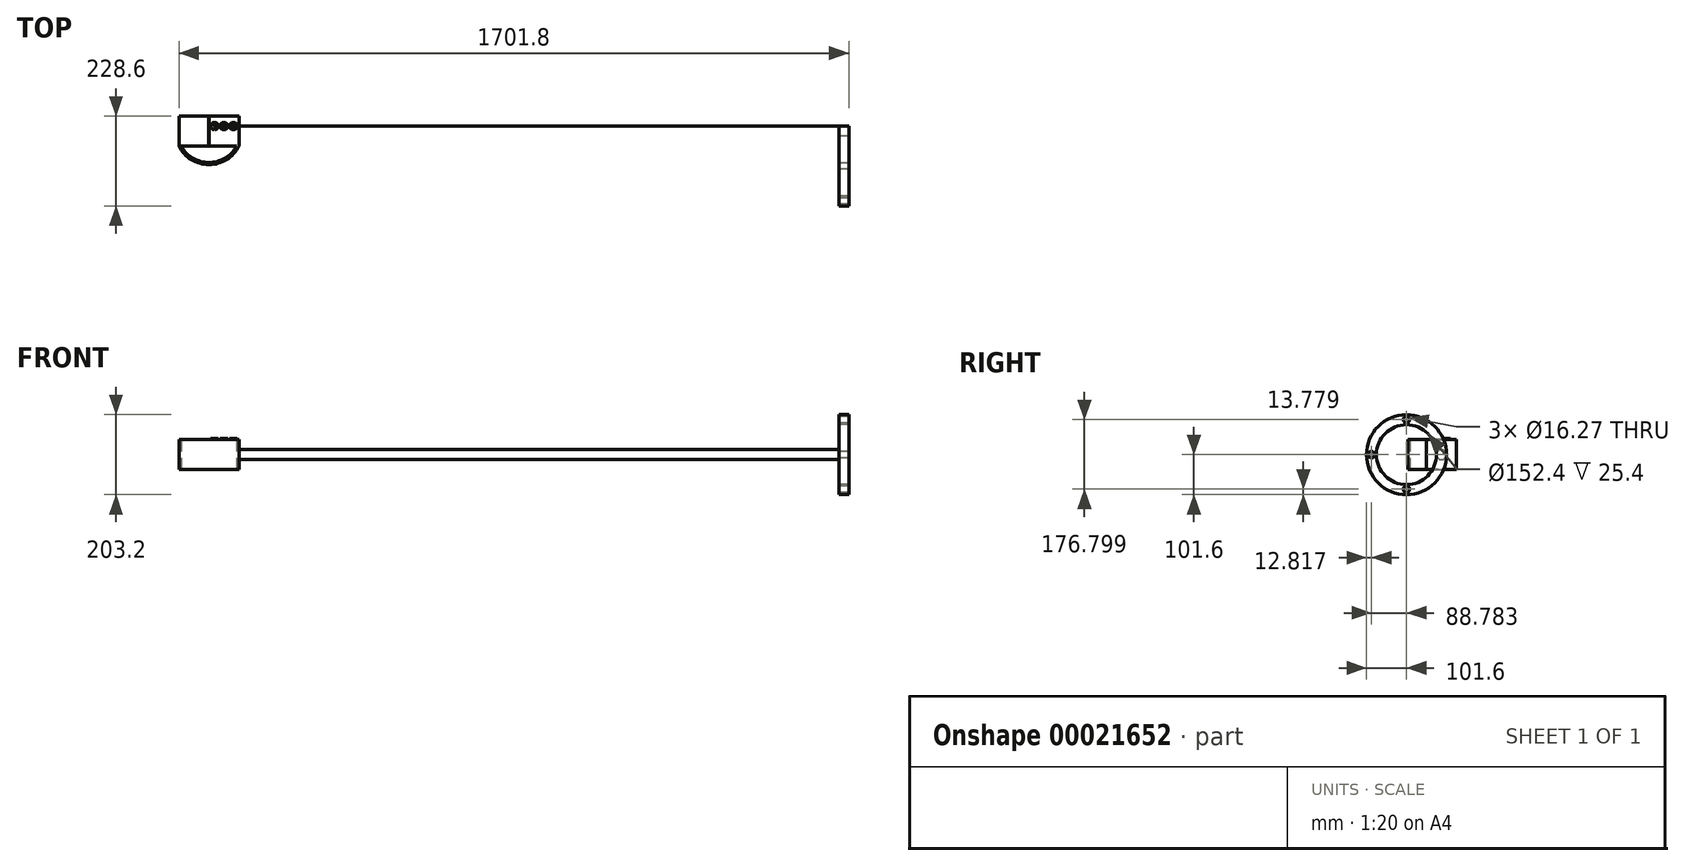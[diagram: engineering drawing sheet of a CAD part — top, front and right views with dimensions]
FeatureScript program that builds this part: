
annotation { "Feature Type Name" : "Feature", "Feature Type Description" : "" }
export const myFeature = defineFeature(function(context is Context, id is Id, definition is map)
    precondition{}
    {
        {
            var Q0;
            Q0=qCreatedBy(makeId("Top.planeOp"),FACE);
            var sketch = newSketch(context, id + "F0", { "sketchPlane" : qUnion([Q0])});
            skLineSegment(sketch, "E0", {"start": v(5.75, 0) * mm, "end": v(146.65, 0) * mm});
            skLineSegment(sketch, "E1", {"start": v(152.4, 0) * mm, "end": v(152.4, 76.2) * mm});
            skLineSegment(sketch, "E2", {"start": v(152.4, 76.2) * mm, "end": v(0, 76.2) * mm});
            skLineSegment(sketch, "E3", {"start": v(0, 76.2) * mm, "end": v(0, 0) * mm});
            skArc(sketch, "E4", {"start": v(0, 0) * mm, "mid": v(76.2, -47.1) * mm, "end": v(152.4, 0) * mm});
            skArc(sketch, "E5", {"start": v(5.75, 0) * mm, "mid": v(76.2, -41.99) * mm, "end": v(146.65, 0) * mm});
            skSolve(sketch);
        }
        {
            var Q0;
            Q0 = qSketchRegion(id + "F0", true);
            extrude(context, id + "F1", {"entities" : qUnion([Q0]), "depth" : 76.2 * mm});
        }
        {
            var Q0;
            Q0=makeQuery(id+"F1.opExtrude","SWEPT_FACE",FACE,{"disambiguationData":[OSD([sQuery(id+"F0.wireOp",EDGE,"E1")])]});
            var sketch = newSketch(context, id + "F2", { "sketchPlane" : qUnion([Q0])});
            skLineSegment(sketch, "E6", {"start": v(76.2, 76.2) * mm, "end": v(47.08, 47.08) * mm});
            skLineSegment(sketch, "E7", {"start": v(0, 0) * mm, "end": v(29.12, 29.12) * mm});
            skLineSegment(sketch, "E8", {"start": v(76.2, 0) * mm, "end": v(47.08, 29.12) * mm});
            skCircle(sketch, "E9", {"center": v(38.1, 38.1) * mm, "radius": 12.7 * mm});
            skLineSegment(sketch, "E10.trimOffspring", {"start": v(47.08, 47.08) * mm, "end": v(76.2, 76.2) * mm});
            skLineSegment(sketch, "E11.trimOffspring", {"start": v(29.12, 29.12) * mm, "end": v(0, 0) * mm});
            skLineSegment(sketch, "E12.trimOffspring", {"start": v(29.12, 47.08) * mm, "end": v(0, 76.2) * mm});
            skSolve(sketch);
        }
        {
            var Q0;
            {var subQ0=sQuery(id+"F2.wireOp",EDGE,"E9");var subQ1=makeQuery(id+"F2.imprint","INTERSECT",VERTEX,{"derivedFrom":[subQ0,sQuery(id+"F2.wireOp",EDGE,"E10.trimOffspring")]});Q0=makeQuery(id+"F2.imprint","IMPRINT",FACE,{"disambiguationData":[TD([[makeQuery(id+"F2.imprint","IMPRINT",EDGE,{"disambiguationData":[TD([[subQ1,-1.0]])],"derivedFrom":subQ0}),1.0]])]});}
            extrude(context, id + "F3", {"entities" : qUnion([Q0]), "operationType" : NewBodyOperationType.ADD, "depth" : 1524 * mm});
        }
        {
            var Q0;
            Q0=makeQuery(id+"F3.opExtrude","CAP_FACE",FACE,{"disambiguationData":[OSD([sQuery(id+"F2.wireOp",EDGE,"E9")])],"isStart":false});
            var sketch = newSketch(context, id + "F4", { "sketchPlane" : qUnion([Q0])});
            skLineSegment(sketch, "E13", {"start": v(38.1, 38.1) * mm, "end": v(50.8, 38.1) * mm});
            skLineSegment(sketch, "E14", {"start": v(50.8, 38.1) * mm, "end": v(-50.8, 38.1) * mm});
            skCircle(sketch, "E15", {"center": v(-50.8, 38.1) * mm, "radius": 101.6 * mm});
            skCircle(sketch, "E16", {"center": v(-50.8, 38.1) * mm, "radius": 76.2 * mm});
            skCircle(sketch, "E17", {"center": v(-50.8, 127.08) * mm, "radius": 8.14 * mm});
            skCircle(sketch, "E18", {"center": v(-139.58, 38.1) * mm, "radius": 8.14 * mm});
            skCircle(sketch, "E19", {"center": v(-50.8, -49.72) * mm, "radius": 8.14 * mm});
            skSolve(sketch);
        }
        {
            var Q0;
            Q0 = qSketchRegion(id + "F4", true);
            extrude(context, id + "F5", {"entities" : qUnion([Q0]), "operationType" : NewBodyOperationType.ADD, "depth" : 25.4 * mm});
        }
        {
            var Q0;
            Q0=makeQuery(id+"F1.opExtrude","CAP_FACE",FACE,{"disambiguationData":[OSD([sQuery(id+"F0.wireOp",EDGE,"E0"),sQuery(id+"F0.wireOp",EDGE,"E1"),sQuery(id+"F0.wireOp",EDGE,"E2"),sQuery(id+"F0.wireOp",EDGE,"E3"),sQuery(id+"F0.wireOp",EDGE,"E4"),sQuery(id+"F0.wireOp",EDGE,"E5")])],"isStart":false});
            var sketch = newSketch(context, id + "F6", { "sketchPlane" : qUnion([Q0])});
            skLineSegment(sketch, "E20", {"start": v(76.2, 76.2) * mm, "end": v(76.2, 0) * mm});
            skLineSegment(sketch, "E21", {"start": v(152.4, 76.2) * mm, "end": v(152.4, 50.8) * mm});
            skLineSegment(sketch, "E22", {"start": v(152.4, 50.8) * mm, "end": v(152.4, 76.2) * mm});
            skLineSegment(sketch, "E23", {"start": v(76.2, 76.2) * mm, "end": v(152.4, 76.2) * mm});
            skCircle(sketch, "E24", {"center": v(90.49, 50.8) * mm, "radius": 9.53 * mm});
            skCircle(sketch, "E25", {"center": v(138.11, 50.8) * mm, "radius": 9.53 * mm});
            skCircle(sketch, "E26", {"center": v(114.3, 50.8) * mm, "radius": 9.53 * mm});
            skText(sketch, "E27", { "text": "S", "fontName": "OpenSans-Regular.ttf"});
            skLineSegment(sketch, "E28", {"start": v(152.4, 50.8) * mm, "end": v(76.2, 50.8) * mm});
            skLineSegment(sketch, "E29", {"start": v(76.2, 50.8) * mm, "end": v(152.4, 50.8) * mm});
            skText(sketch, "E30", { "text": "V", "fontName": "OpenSans-Regular.ttf"});
            skText(sketch, "E31", { "text": "N\n", "fontName": "OpenSans-Regular.ttf"});
            skLineSegment(sketch, "E32", {"start": v(76.2, 76.2) * mm, "end": v(75.95, 76.2) * mm});
            skLineSegment(sketch, "E33", {"start": v(75.95, 76.2) * mm, "end": v(75.95, 0) * mm});
            skCircle(sketch, "E34", {"center": v(100.6, 34.59) * mm, "radius": 3.97 * mm});
            skCircle(sketch, "E35", {"center": v(111.76, 34.59) * mm, "radius": 3.97 * mm});
            skCircle(sketch, "E36", {"center": v(122.92, 34.59) * mm, "radius": 3.97 * mm});
            skCircle(sketch, "E37", {"center": v(100.6, 23.6) * mm, "radius": 3.97 * mm});
            skCircle(sketch, "E38", {"center": v(100.6, 12.61) * mm, "radius": 3.97 * mm});
            skCircle(sketch, "E39", {"center": v(111.76, 12.61) * mm, "radius": 3.97 * mm});
            skCircle(sketch, "E40", {"center": v(111.76, 23.6) * mm, "radius": 3.97 * mm});
            skCircle(sketch, "E41", {"center": v(122.92, 23.6) * mm, "radius": 3.97 * mm});
            skCircle(sketch, "E42", {"center": v(122.92, 12.61) * mm, "radius": 3.97 * mm});
            const initialGuessF6  = {"E27": [0.08688, 0.0455, 1, 0, 0.0108], "E30": [0.11016, 0.04563, 1, 0, 0.01047], "E31": [0.1332, 0.0455, 1, 0, 0.01061]};
            skSetInitialGuess(sketch, initialGuessF6);
            skSolve(sketch);
        }
        {
            var Q0;
            {var subQ9=sQuery(id+"F6.wireOp",EDGE,"E27.sketch_text.stroke-12");Q0=makeQuery(id+"F6.imprint","IMPRINT",FACE,{"disambiguationData":[TD([[makeQuery(id+"F6.imprint","IMPRINT",EDGE,{"derivedFrom":subQ9}),1.0]])]});}
            var Q1;
            Q1=makeQuery(id+"F6.imprint","IMPRINT",FACE,{"disambiguationData":[TD([[makeQuery(id+"F6.imprint","IMPRINT",EDGE,{"derivedFrom":sQuery(id+"F6.wireOp",EDGE,"E27.sketch_text.stroke-0")}),1.0]])]});
            var Q2;
            {var subQ8=sQuery(id+"F6.wireOp",EDGE,"E30.sketch_text.stroke-0");Q2=makeQuery(id+"F6.imprint","IMPRINT",FACE,{"disambiguationData":[TD([[makeQuery(id+"F6.imprint","IMPRINT",EDGE,{"derivedFrom":subQ8}),1.0]])]});}
            var Q3;
            {var subQ3=sQuery(id+"F6.wireOp",EDGE,"E30.sketch_text.stroke-2");Q3=makeQuery(id+"F6.imprint","IMPRINT",FACE,{"disambiguationData":[TD([[makeQuery(id+"F6.imprint","IMPRINT",EDGE,{"derivedFrom":subQ3}),1.0]])]});}
            var Q4;
            {var subQ4=sQuery(id+"F6.wireOp",EDGE,"E31.sketch_text.stroke-7");Q4=makeQuery(id+"F6.imprint","IMPRINT",FACE,{"disambiguationData":[TD([[makeQuery(id+"F6.imprint","IMPRINT",EDGE,{"derivedFrom":subQ4}),1.0]])]});}
            var Q5;
            {var subQ3=sQuery(id+"F6.wireOp",EDGE,"E31.sketch_text.stroke-0");Q5=makeQuery(id+"F6.imprint","IMPRINT",FACE,{"disambiguationData":[TD([[makeQuery(id+"F6.imprint","IMPRINT",EDGE,{"derivedFrom":subQ3}),1.0]])]});}
            extrude(context, id + "F7", {"entities" : qUnion([Q0, Q1, Q2, Q3, Q4, Q5]), "operationType" : NewBodyOperationType.ADD, "depth" : 2.54 * mm});
        }
        {
            var Q0;
            {var subQ4=sQuery(id+"F6.wireOp",EDGE,"E32");Q0=makeQuery(id+"F6.imprint","IMPRINT",FACE,{"disambiguationData":[TD([[makeQuery(id+"F6.imprint","IMPRINT",EDGE,{"derivedFrom":subQ4}),1.0]])]});}
            extrude(context, id + "F8", {"entities" : qUnion([Q0]), "operationType" : NewBodyOperationType.ADD, "depth" : 0.1 * mm});
        }
        {
            var Q0;
            Q0=sQuery(id+"F6.wireOp",EDGE,"E34");
            var Q1;
            Q1=sQuery(id+"F6.wireOp",EDGE,"E35");
            var Q2;
            Q2=sQuery(id+"F6.wireOp",EDGE,"E36");
            var Q3;
            Q3=sQuery(id+"F6.wireOp",EDGE,"E41");
            var Q4;
            Q4=sQuery(id+"F6.wireOp",EDGE,"E40");
            var Q5;
            Q5=sQuery(id+"F6.wireOp",EDGE,"E37");
            var Q6;
            Q6=sQuery(id+"F6.wireOp",EDGE,"E38");
            var Q7;
            Q7=sQuery(id+"F6.wireOp",EDGE,"E39");
            var Q8;
            Q8=sQuery(id+"F6.wireOp",EDGE,"E42");
            extrude(context, id + "F9", {"bodyType" : ToolBodyType.SURFACE, "surfaceEntities" : qUnion([Q0, Q1, Q2, Q3, Q4, Q5, Q6, Q7, Q8]), "oppositeDirection" : true, "depth" : 6.35 * mm});
        }
        {
            var Q0;
            Q0=sQuery(id+"F4.wireOp",EDGE,"E17");
            var Q1;
            Q1=sQuery(id+"F4.wireOp",EDGE,"E18");
            var Q2;
            Q2=sQuery(id+"F4.wireOp",EDGE,"E19");
            extrude(context, id + "F10", {"bodyType" : ToolBodyType.SURFACE, "surfaceEntities" : qUnion([Q0, Q1, Q2]), "depth" : 30.64 * mm});
        }
        {
            var Q0;
            {var subQ0=sQuery(id+"F0.wireOp",EDGE,"E0");var subQ1=sQuery(id+"F0.wireOp",EDGE,"E1");var subQ2=sQuery(id+"F0.wireOp",EDGE,"E2");var subQ3=sQuery(id+"F0.wireOp",EDGE,"E3");var subQ4=sQuery(id+"F0.wireOp",EDGE,"E4");var subQ5=sQuery(id+"F0.wireOp",EDGE,"E5");Q0=makeQuery(id+"F7.boolean.opBoolean","SPLIT",FACE,{"disambiguationData":[TD([makeQuery(id+"F1.opExtrude","SWEPT_FACE",FACE,{"disambiguationData":[OSD([subQ0])]})])],"derivedFrom":makeQuery(id+"F1.opExtrude","CAP_FACE",FACE,{"disambiguationData":[OSD([subQ0,subQ1,subQ2,subQ3,subQ4,subQ5])],"isStart":false})});}
            extrude(context, id + "F11", {"entities" : qUnion([Q0]), "operationType" : NewBodyOperationType.ADD, "oppositeDirection" : true, "depth" : 2.54 * mm});
        }
    });
